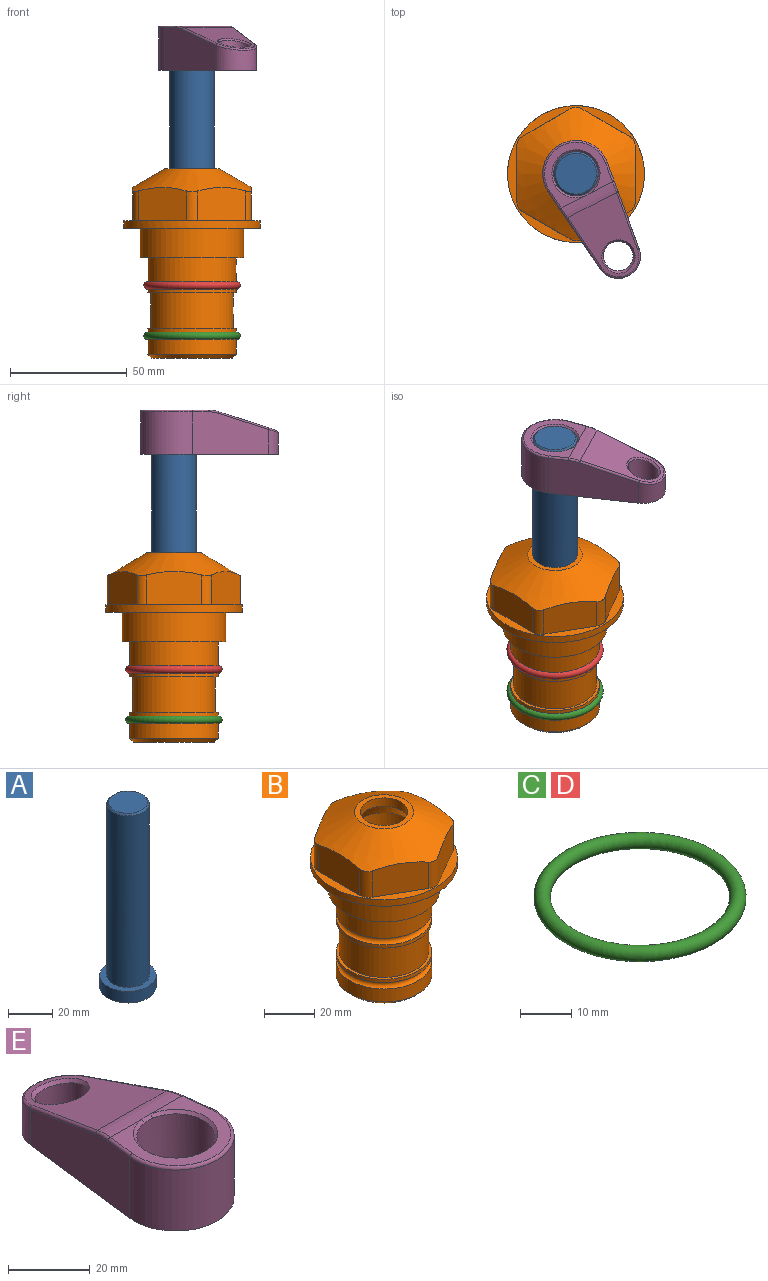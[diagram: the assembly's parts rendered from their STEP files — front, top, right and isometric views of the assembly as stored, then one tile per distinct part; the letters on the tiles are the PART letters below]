
ASSEMBLY  parts=5 mates=4
PART A: 6 faces, bbox 25.4x25.4x101.6 mm
  f0: plane 17.46x17.46mm, normal (0,0,1), area 239.5mm2, adj f5
  f1: plane 25.4x25.4mm, normal (0,0,-1), area 506.7mm2, adj f2
  f2: cylinder r=12.7mm len=25.4mm, axis (0,0,1), area 506.7mm2, adj f1,f3
  f3: plane 25.4x25.4mm, normal (0,0,1), area 221.7mm2, adj f2,f4
  f4: cylinder r=9.53mm len=94.46mm, axis (0,0,1), area 5653mm2, adj f3,f5
  f5: cone r=8.73mm half-angle=45deg, axis (0,0,-1), area 64.4mm2, adj f0,f4
PART B: 36 faces, bbox 58.7x58.7x81 mm
  f0: cylinder r=17.78mm len=35.56mm, axis (0,0,1), area 1670.8mm2, adj f23,f24,f31
  f1: cylinder r=19.05mm len=38.1mm, axis (0,0,1), area 1191.9mm2, adj f26,f27,f30
  f2: plane 58.66x58.66mm, normal (0,0,-1), area 1150.6mm2, adj f3,f28
  f3: cylinder r=29.33mm len=58.66mm, axis (0,0,-1), area 585.1mm2, adj f2,f4
  f4: plane 58.66x58.66mm, normal (0,0,1), area 475.9mm2, adj f3,f5,f6,f7,f8,f9,f10,f11
  f5: plane 20.32x14.34mm, normal (-0.5,0.87,0), area 324.4mm2, adj f4,f15,f16,f17
  f6: plane 20.32x14.34mm, normal (0.5,0.87,0), area 324.4mm2, adj f4,f14,f15,f17
  f7: plane 23.48x14.34mm, normal (1,0,0), area 324.4mm2, adj f4,f13,f14,f17
  f8: plane 20.32x14.34mm, normal (0.5,-0.87,0), area 324.4mm2, adj f4,f12,f13,f17
  f9: plane 20.32x14.34mm, normal (-0.5,-0.87,0), area 324.4mm2, adj f4,f11,f12,f17
  f10: plane 23.48x14.34mm, normal (-1,0,0), area 324.4mm2, adj f4,f11,f16,f17
  f11: cylinder r=5.08mm len=12.85mm, axis (0,0,-1), area 67.2mm2, adj f4,f9,f10,f17
  f12: cylinder r=5.08mm len=12.85mm, axis (0,0,-1), area 67.2mm2, adj f4,f8,f9,f17
  f13: cylinder r=5.08mm len=12.85mm, axis (0,0,-1), area 67.2mm2, adj f4,f7,f8,f17
  f14: cylinder r=5.08mm len=12.85mm, axis (0,0,-1), area 67.2mm2, adj f4,f6,f7,f17
  f15: cylinder r=5.08mm len=12.85mm, axis (0,0,-1), area 67.2mm2, adj f4,f5,f6,f17
  f16: cylinder r=5.08mm len=12.85mm, axis (0,0,-1), area 67.2mm2, adj f4,f5,f10,f17
  f17: cone r=11.73mm half-angle=60deg, axis (0,0,-1), area 2071.8mm2, adj f5,f6,f7,f8,f9,f10,f11,f12
  f18: plane 23.46x23.46mm, normal (0,0,1), area 147.4mm2, adj f17,f35
  f19: plane 34.93x34.93mm, normal (0,0,-1), area 958mm2, adj f29
  f20: cylinder r=19.05mm len=38.1mm, axis (0,0,1), area 760.1mm2, adj f21,f29
  f21: torus R=19.05mm, axis (0,0,1), area 565.3mm2, adj f20,f22
  f22: cylinder r=19.05mm len=38.1mm, axis (0,0,1), area 190mm2, adj f21,f23
  f23: plane 38.1x38.1mm, normal (0,0,1), area 146.9mm2, adj f0,f22
  f24: plane 38.1x38.1mm, normal (0,0,-1), area 146.9mm2, adj f0,f25
  f25: cylinder r=19.05mm len=38.1mm, axis (0,0,1), area 190mm2, adj f24,f26
  f26: torus R=19.05mm, axis (0,0,1), area 565.3mm2, adj f1,f25
  f27: plane 44.45x44.45mm, normal (0,0,-1), area 411.7mm2, adj f1,f28
  f28: cylinder r=22.23mm len=44.45mm, axis (0,0,1), area 1773.5mm2, adj f2,f27
  f29: cone r=19.05mm half-angle=45deg, axis (0,0,1), area 257.5mm2, adj f19,f20
  f30: cylinder r=3.17mm len=6.75mm, axis (-1,0,0), area 128mm2, adj f1,f33
  f31: cylinder r=3.17mm len=6.35mm, axis (-1,0,0), area 102.5mm2, adj f0,f33
  f32: plane 25.4x25.4mm, normal (0,0,1), area 506.7mm2, adj f33
  f33: cylinder r=12.7mm len=66.42mm, axis (0,0,-1), area 5236.2mm2, adj f30,f31,f32,f34
  f34: cone r=9.53mm half-angle=30deg, axis (0,0,-1), area 443.4mm2, adj f33,f35
  f35: cylinder r=9.53mm len=19.05mm, axis (0,0,-1), area 240.9mm2, adj f18,f34
PART C: 1 faces, bbox 44.7x44.7x3.2 mm
  f0: torus R=19.05mm, axis (0,0,1), area 1193.9mm2
PART D: same geometry as C
PART E: 31 faces, bbox 31.7x65.5x19.8 mm
  f0: plane 39.12x18.26mm, normal (0.99,0.12,0), area 612.2mm2, adj f1,f4,f7,f11,f13,f15
  f1: cylinder r=9.53mm len=18.91mm, axis (0,0,-1), area 296.1mm2, adj f0,f2,f7,f17
  f2: plane 39.12x18.26mm, normal (-0.99,0.12,0), area 612.2mm2, adj f1,f4,f7,f12,f14,f16
  f3: cylinder r=6.35mm len=12.7mm, axis (0,0,-1), area 362.4mm2, adj f7,f18
  f4: cylinder r=14.29mm len=28.58mm, axis (0,0,-1), area 882.2mm2, adj f0,f2,f7,f10
  f5: cylinder r=9.53mm len=19.05mm, axis (0,0,-1), area 1092.6mm2, adj f7,f19,f20
  f6: plane 26.99x23.69mm, normal (0,0,1), area 216.2mm2, adj f9,f10,f11,f12,f19
  f7: plane 63.5x28.58mm, normal (0,0,-1), area 661.8mm2, adj f0,f1,f2,f3,f4,f5,f22,f23
  f8: plane 33.52x23.6mm, normal (0,0.26,0.97), area 486mm2, adj f9,f15,f16,f17,f18
  f9: cylinder r=19.05mm len=24.72mm, axis (1,0,0), area 120.4mm2, adj f6,f8,f13,f14,f20
  f10: torus R=13.49mm, axis (0,0,1), area 59mm2, adj f4,f6,f11,f12
  f11: cylinder r=0.79mm len=8.67mm, axis (0.12,-0.99,0), area 10.8mm2, adj f0,f6,f10,f13
  f12: cylinder r=0.79mm len=8.67mm, axis (0.12,0.99,0), area 10.8mm2, adj f2,f6,f10,f14
  f13: bspline ~4.95x1.42mm, area 6.1mm2, adj f0,f9,f11,f15
  f14: bspline ~4.95x1.42mm, area 6.1mm2, adj f2,f9,f12,f16
  f15: cylinder r=0.79mm len=25.95mm, axis (0.12,-0.96,0.26), area 32.9mm2, adj f0,f8,f13,f17
  f16: cylinder r=0.79mm len=25.95mm, axis (0.12,0.96,-0.26), area 32.9mm2, adj f2,f8,f14,f17
  f17: bspline ~18.91x8.38mm, area 30mm2, adj f1,f8,f15,f16
  f18: bspline ~14.29x14.29mm, area 48.3mm2, adj f3,f8
  f19: cone r=9.53mm half-angle=45deg, axis (0,0,1), area 66.5mm2, adj f5,f6,f20
  f20: bspline ~3.22x0.96mm, area 3.5mm2, adj f5,f9,f19
  f21: plane 2.75x2.72mm, normal (0,0,-1), area 2.9mm2, adj f23,f25,f28
  f22: plane 23.05x15.88mm, normal (-0.99,-0.12,0), area 323.6mm2, adj f7,f25,f26,f27,f28,f29
  f23: plane 23.05x15.88mm, normal (0.99,-0.12,0), area 323.6mm2, adj f7,f21,f25,f27,f28,f30
  f24: cylinder r=9.53mm len=10.69mm, axis (0,0,-1), area 114.7mm2, adj f7,f27,f29,f30
  f25: cylinder r=12.7mm len=20.59mm, axis (0,0,-1), area 381.1mm2, adj f7,f21,f22,f23,f26,f28
  f26: plane 2.75x2.72mm, normal (0,0,-1), area 2.9mm2, adj f22,f25,f28
  f27: plane 19.72x18.37mm, normal (0,-0.26,-0.97), area 291.8mm2, adj f22,f23,f24,f28,f29,f30
  f28: cylinder r=15.88mm len=19.92mm, axis (1,0,0), area 54.8mm2, adj f21,f22,f23,f25,f26,f27
  f29: cylinder r=1.59mm len=11mm, axis (0,0,-1), area 34.7mm2, adj f7,f22,f24,f27
  f30: cylinder r=1.59mm len=11mm, axis (0,0,-1), area 34.7mm2, adj f7,f23,f24,f27
PLACE A rot(axis=(0,0,-1),152.8deg) t=(0,0,23.2)mm
PLACE B at identity fixed
PLACE C t=(0,0,-21.59)mm
PLACE D at identity
PLACE E rot(axis=(0,0,-1),152.8deg) t=(0,0,23.2)mm
MATE fastened C.f0 <-> B.f0  axis (0,0,1) through (0,0,-46.1)mm
MATE fastened E.f4 <-> A.f2  axis (0,0,1) through (0,0,86.7)mm
MATE fastened D.f0 <-> B.f0  axis (0,0,1) through (0,0,-24.51)mm
MATE cylindrical B.f0 <-> A.f2  axis (0,0,-1) through (0,0,21.37)mm
